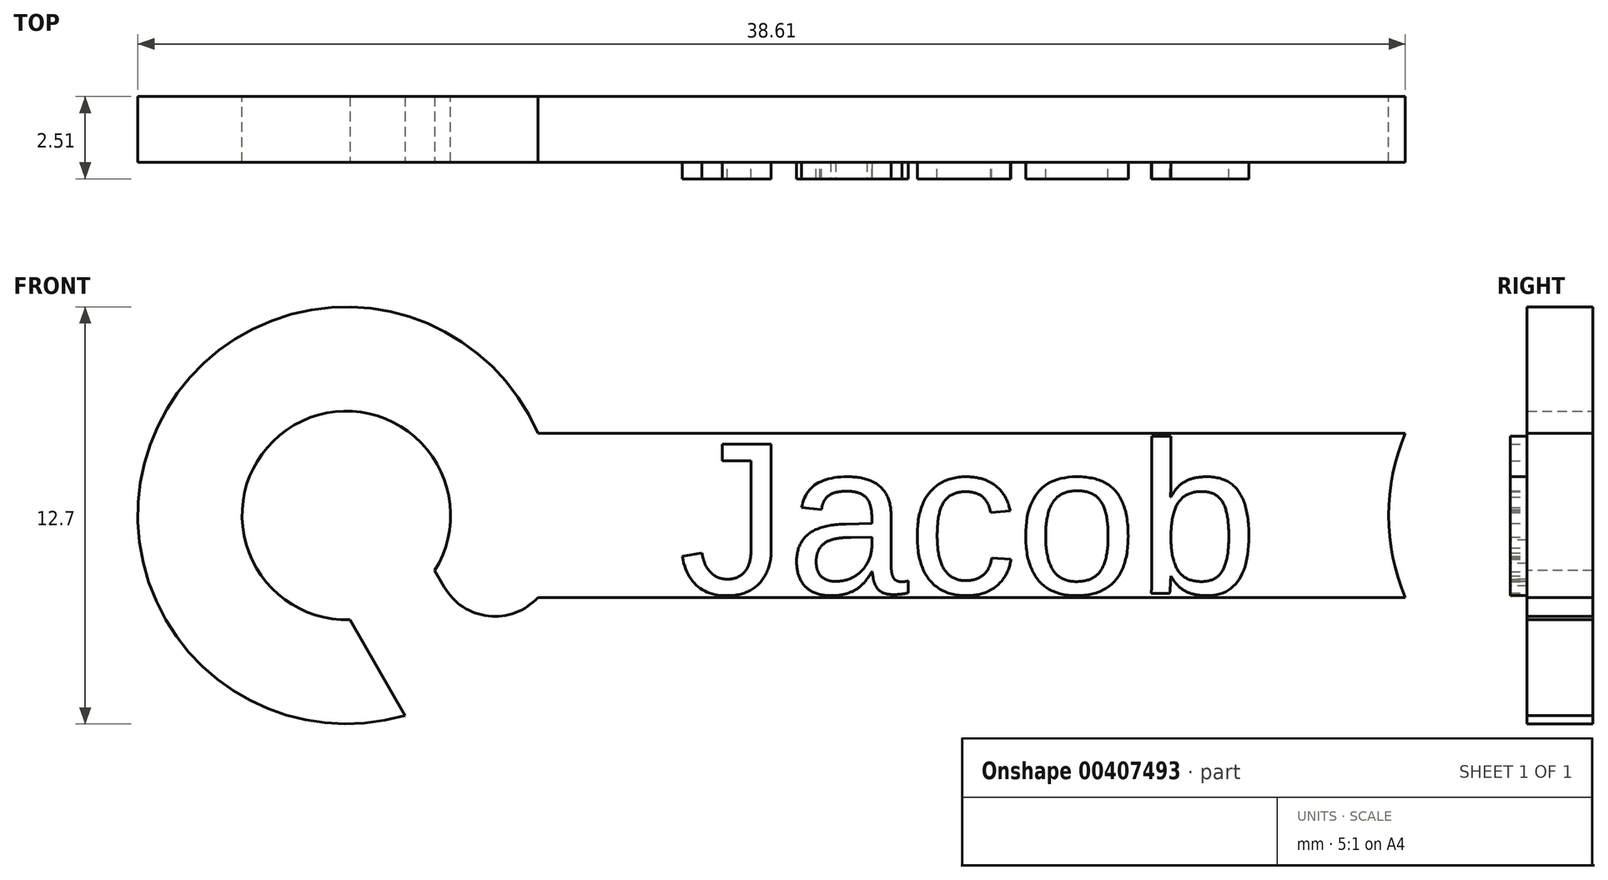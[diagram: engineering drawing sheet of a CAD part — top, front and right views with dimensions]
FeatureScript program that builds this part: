
annotation { "Feature Type Name" : "Feature", "Feature Type Description" : "" }
export const myFeature = defineFeature(function(context is Context, id is Id, definition is map)
    precondition{}
    {
        {
            var Q0;
            Q0=qCreatedBy(makeId("Front.planeOp"),FACE);
            var sketch = newSketch(context, id + "F0", { "sketchPlane" : qUnion([Q0])});
            skCircle(sketch, "E0", {"center": v(-19.05, 0) * mm, "radius": 6.35 * mm});
            skLineSegment(sketch, "E1", {"start": v(-13.21, 2.5) * mm, "end": v(0, 2.5) * mm});
            skLineSegment(sketch, "E2.MirrorCS", {"start": v(-13.21, -2.5) * mm, "end": v(0, -2.5) * mm});
            skLineSegment(sketch, "E3.MirrorCS", {"start": v(13.21, 2.5) * mm, "end": v(0, 2.5) * mm});
            skLineSegment(sketch, "E4.MirrorCS", {"start": v(13.21, -2.5) * mm, "end": v(0, -2.5) * mm});
            skCircle(sketch, "E5.MirrorC", {"center": v(19.05, 0) * mm, "radius": 6.35 * mm});
            skCircle(sketch, "E6", {"center": v(-19.05, 0) * mm, "radius": 3.18 * mm});
            skCircle(sketch, "E7.MirrorC", {"center": v(19.05, 0) * mm, "radius": 3.18 * mm});
            skSolve(sketch);
        }
        {
            var Q0;
            {var subQ0=sQuery(id+"F0.wireOp",EDGE,"E0");var subQ1=makeQuery(id+"F0.imprint","INTERSECT",VERTEX,{"derivedFrom":[subQ0,sQuery(id+"F0.wireOp",EDGE,"E1")]});Q0=makeQuery(id+"F0.imprint","IMPRINT",FACE,{"disambiguationData":[TD([[makeQuery(id+"F0.imprint","IMPRINT",EDGE,{"disambiguationData":[TD([[subQ1,-1.0]])],"derivedFrom":subQ0}),1.0]])]});}
            var Q1;
            {var subQ2=sQuery(id+"F0.wireOp",EDGE,"E1");Q1=makeQuery(id+"F0.imprint","IMPRINT",FACE,{"disambiguationData":[TD([[makeQuery(id+"F0.imprint","IMPRINT",EDGE,{"derivedFrom":subQ2}),-1.0]])]});}
            var Q2;
            {var subQ0=sQuery(id+"F0.wireOp",EDGE,"E5.MirrorC");var subQ1=makeQuery(id+"F0.imprint","INTERSECT",VERTEX,{"derivedFrom":[sQuery(id+"F0.wireOp",EDGE,"E3.MirrorCS"),subQ0]});Q2=makeQuery(id+"F0.imprint","IMPRINT",FACE,{"disambiguationData":[TD([[makeQuery(id+"F0.imprint","IMPRINT",EDGE,{"disambiguationData":[TD([[subQ1,-1.0]])],"derivedFrom":subQ0}),-1.0]])]});}
            extrude(context, id + "F1", {"entities" : qUnion([Q0, Q1, Q2]), "endBound" : BoundingType.SYMMETRIC, "depth" : 2 * mm, "offsetDistance" : 25.4 * mm});
        }
        {
            var Q0;
            Q0=qCreatedBy(makeId("Front.planeOp"),FACE);
            var sketch = newSketch(context, id + "F2", { "sketchPlane" : qUnion([Q0])});
            skArc(sketch, "E8.0", {"start": v(-18.94, -3.17) * mm, "mid": v(-17.46, -2.75) * mm, "end": v(-16.36, -1.68) * mm});
            skArc(sketch, "E9.0", {"start": v(-17.26, -6.1) * mm, "mid": v(-15.88, -5.5) * mm, "end": v(-14.67, -4.6) * mm});
            skLineSegment(sketch, "E10", {"start": v(-19.05, 0) * mm, "end": v(-15.88, -5.5) * mm, "construction": true});
            skLineSegment(sketch, "E11", {"start": v(-16.36, -1.68) * mm, "end": v(-14.67, -4.6) * mm});
            skLineSegment(sketch, "E12.MirrorCS", {"start": v(-18.94, -3.17) * mm, "end": v(-17.26, -6.1) * mm});
            skArc(sketch, "E13", {"start": v(-14.67, -4.6) * mm, "mid": v(-15.88, -5.5) * mm, "end": v(-17.26, -6.1) * mm});
            skPoint(sketch, "E14.orphan", {"position": v(-17.32, 0) * mm});
            skPoint(sketch, "E15.orphan", {"position": v(-19.91, -1.5) * mm});
            skPoint(sketch, "E16.orphan", {"position": v(-13.21, 2.5) * mm});
            skPoint(sketch, "E17.orphan", {"position": v(-13.21, -2.5) * mm});
            skArc(sketch, "E18.MirrorCS", {"start": v(17.26, -6.1) * mm, "mid": v(15.88, -5.5) * mm, "end": v(14.67, -4.6) * mm});
            skArc(sketch, "E19.MirrorCS", {"start": v(14.67, -4.6) * mm, "mid": v(15.88, -5.5) * mm, "end": v(17.26, -6.1) * mm});
            skArc(sketch, "E20.MirrorCS", {"start": v(18.94, -3.17) * mm, "mid": v(17.46, -2.75) * mm, "end": v(16.36, -1.68) * mm});
            skLineSegment(sketch, "E21.MirrorCS", {"start": v(16.36, -1.68) * mm, "end": v(14.67, -4.6) * mm});
            skLineSegment(sketch, "E22.MirrorCS", {"start": v(18.94, -3.17) * mm, "end": v(17.26, -6.1) * mm});
            skSolve(sketch);
        }
        {
            var Q0;
            Q0 = qSketchRegion(id + "F2", true);
            extrude(context, id + "F3", {"entities" : qUnion([Q0]), "operationType" : NewBodyOperationType.REMOVE, "endBound" : BoundingType.THROUGH_ALL, "oppositeDirection" : true, "depth" : 25.4 * mm, "offsetDistance" : 25.4 * mm, "hasSecondDirection" : true, "secondDirectionBound" : SecondDirectionBoundingType.THROUGH_ALL, "secondDirectionOppositeDirection" : false, "secondDirectionDepth" : 25.4 * mm});
        }
        {
            var Q0;
            Q0=makeQuery(id+"F3.boolean.opBoolean","COPY",EDGE,{"derivedFrom":makeQuery(id+"F3.opExtrude","SWEPT_EDGE",EDGE,{"disambiguationData":[OSD([sQuery(id+"F2.wireOp",EDGE,"E11"),sQuery(id+"F2.wireOp",EDGE,"E13")])]})});
            var Q1;
            Q1=makeQuery(id+"F3.boolean.opBoolean","COPY",EDGE,{"derivedFrom":makeQuery(id+"F3.opExtrude","SWEPT_EDGE",EDGE,{"disambiguationData":[OSD([sQuery(id+"F2.wireOp",EDGE,"E8.0"),sQuery(id+"F2.wireOp",EDGE,"E11")])]})});
            var Q2;
            Q2=makeQuery(id+"F3.boolean.opBoolean","COPY",EDGE,{"derivedFrom":makeQuery(id+"F3.opExtrude","SWEPT_EDGE",EDGE,{"disambiguationData":[OSD([sQuery(id+"F2.wireOp",EDGE,"E12.MirrorCS"),sQuery(id+"F2.wireOp",EDGE,"E13")])]})});
            var Q3;
            Q3=makeQuery(id+"F3.boolean.opBoolean","COPY",EDGE,{"derivedFrom":makeQuery(id+"F3.opExtrude","SWEPT_EDGE",EDGE,{"disambiguationData":[OSD([sQuery(id+"F2.wireOp",EDGE,"E8.0"),sQuery(id+"F2.wireOp",EDGE,"E12.MirrorCS")])]})});
            var Q4;
            Q4=makeQuery(id+"F3.boolean.opBoolean","COPY",EDGE,{"derivedFrom":makeQuery(id+"F3.opExtrude","SWEPT_EDGE",EDGE,{"disambiguationData":[OSD([sQuery(id+"F2.wireOp",EDGE,"E20.MirrorCS"),sQuery(id+"F2.wireOp",EDGE,"E21.MirrorCS")])]})});
            var Q5;
            Q5=makeQuery(id+"F3.boolean.opBoolean","COPY",EDGE,{"derivedFrom":makeQuery(id+"F3.opExtrude","SWEPT_EDGE",EDGE,{"disambiguationData":[OSD([sQuery(id+"F2.wireOp",EDGE,"E19.MirrorCS"),sQuery(id+"F2.wireOp",EDGE,"E21.MirrorCS")])]})});
            var Q6;
            Q6=makeQuery(id+"F3.boolean.opBoolean","COPY",EDGE,{"derivedFrom":makeQuery(id+"F3.opExtrude","SWEPT_EDGE",EDGE,{"disambiguationData":[OSD([sQuery(id+"F2.wireOp",EDGE,"E20.MirrorCS"),sQuery(id+"F2.wireOp",EDGE,"E22.MirrorCS")])]})});
            var Q7;
            Q7=makeQuery(id+"F3.boolean.opBoolean","COPY",EDGE,{"derivedFrom":makeQuery(id+"F3.opExtrude","SWEPT_EDGE",EDGE,{"disambiguationData":[OSD([sQuery(id+"F2.wireOp",EDGE,"E19.MirrorCS"),sQuery(id+"F2.wireOp",EDGE,"E22.MirrorCS")])]})});
            fillet(context, id + "F4", {"entities" : qUnion([Q0, Q1, Q2, Q3, Q4, Q5, Q6, Q7]), "radius" : 1.78 * mm, "tangentPropagation" : true, "allowEdgeOverflow" : false});
        }
        {
            var Q0;
            Q0=makeQuery(id+"F1.opExtrude","CAP_FACE",FACE,{"disambiguationData":[OSD([sQuery(id+"F0.wireOp",EDGE,"E0"),sQuery(id+"F0.wireOp",EDGE,"E1"),sQuery(id+"F0.wireOp",EDGE,"E2.MirrorCS"),sQuery(id+"F0.wireOp",EDGE,"E3.MirrorCS"),sQuery(id+"F0.wireOp",EDGE,"E4.MirrorCS"),sQuery(id+"F0.wireOp",EDGE,"E5.MirrorC"),sQuery(id+"F0.wireOp",EDGE,"E6"),sQuery(id+"F0.wireOp",EDGE,"E7.MirrorC")])],"isStart":false});
            var sketch = newSketch(context, id + "F5", { "sketchPlane" : qUnion([Q0])});
            skText(sketch, "E23", { "text": "Jacob", "fontName": "Arimo-Regular.ttf"});
            skPoint(sketch, "E24", {"position": v(0, 0) * mm});
            const initialGuessF5  = {"E23": [-0.00892, -0.00238, 1, 0, 0.00476]};
            skSetInitialGuess(sketch, initialGuessF5);
            skSolve(sketch);
        }
        {
            var Q0;
            Q0 = qSketchRegion(id + "F5", true);
            extrude(context, id + "F6", {"entities" : qUnion([Q0]), "operationType" : NewBodyOperationType.ADD, "depth" : 0.5 * mm, "offsetDistance" : 25.4 * mm});
        }
    });
